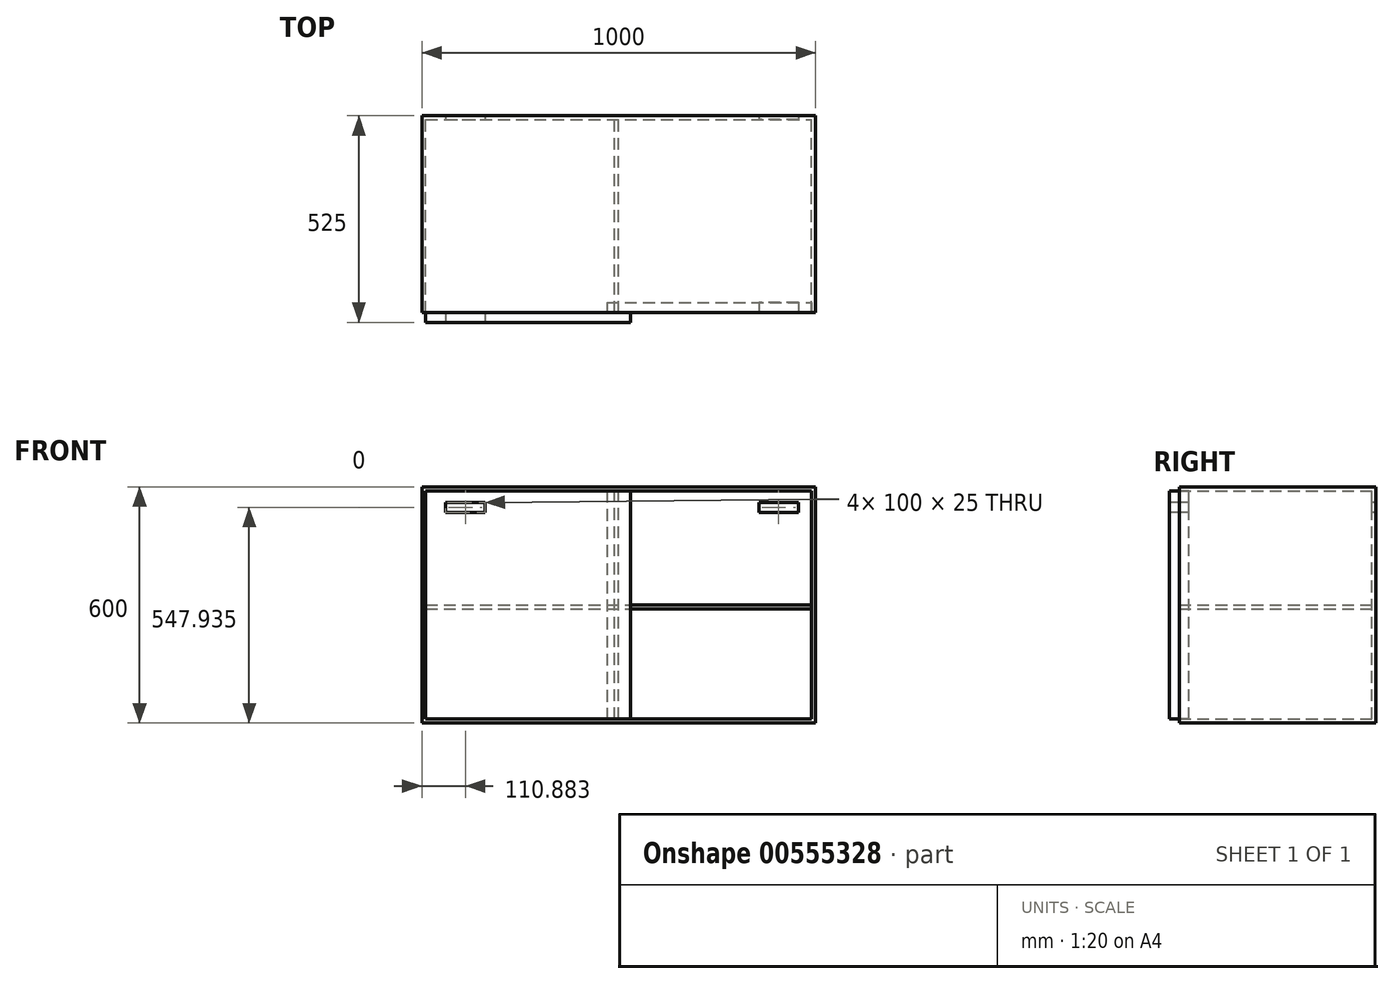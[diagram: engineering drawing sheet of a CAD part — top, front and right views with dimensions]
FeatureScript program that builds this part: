
annotation { "Feature Type Name" : "Feature", "Feature Type Description" : "" }
export const myFeature = defineFeature(function(context is Context, id is Id, definition is map)
    precondition{}
    {
        {
            var Q0;
            Q0=qCreatedBy(makeId("Front.planeOp"),FACE);
            var sketch = newSketch(context, id + "F0", { "sketchPlane" : qUnion([Q0])});
            skLineSegment(sketch, "E0.bottom", {"start": v(0, 0) * mm, "end": v(1000, 0) * mm});
            skLineSegment(sketch, "E0.top", {"start": v(0, 600) * mm, "end": v(1000, 600) * mm});
            skLineSegment(sketch, "E0.left", {"start": v(0, 0) * mm, "end": v(0, 600) * mm});
            skLineSegment(sketch, "E0.right", {"start": v(1000, 0) * mm, "end": v(1000, 600) * mm});
            skSolve(sketch);
        }
        {
            var Q0;
            Q0 = qSketchRegion(id + "F0", true);
            extrude(context, id + "F1", {"entities" : qUnion([Q0]), "depth" : 500 * mm, "offsetDistance" : 25 * mm});
        }
        {
            var Q0;
            Q0=makeQuery(id+"F1.opExtrude","CAP_FACE",FACE,{"disambiguationData":[OSD([sQuery(id+"F0.wireOp",EDGE,"E0.bottom"),sQuery(id+"F0.wireOp",EDGE,"E0.top"),sQuery(id+"F0.wireOp",EDGE,"E0.left"),sQuery(id+"F0.wireOp",EDGE,"E0.right")])],"isStart":false});
            shell(context, id + "F2", {"entities" : qUnion([Q0]), "thickness" : 10 * mm});
        }
        {
            var Q0;
            Q0=makeQuery(id+"F1.opExtrude","CAP_FACE",FACE,{"disambiguationData":[OSD([sQuery(id+"F0.wireOp",EDGE,"E0.bottom"),sQuery(id+"F0.wireOp",EDGE,"E0.top"),sQuery(id+"F0.wireOp",EDGE,"E0.left"),sQuery(id+"F0.wireOp",EDGE,"E0.right")])],"isStart":false});
            var sketch = newSketch(context, id + "F3", { "sketchPlane" : qUnion([Q0])});
            skLineSegment(sketch, "E1.bottom", {"start": v(10, 590) * mm, "end": v(530, 590) * mm});
            skLineSegment(sketch, "E1.top", {"start": v(10, 10) * mm, "end": v(530, 10) * mm});
            skLineSegment(sketch, "E1.left", {"start": v(10, 590) * mm, "end": v(10, 10) * mm});
            skLineSegment(sketch, "E1.right", {"start": v(530, 590) * mm, "end": v(530, 10) * mm});
            skLineSegment(sketch, "E2.bottom", {"start": v(990, 590) * mm, "end": v(470, 590) * mm});
            skLineSegment(sketch, "E2.top", {"start": v(990, 10) * mm, "end": v(470, 10) * mm});
            skLineSegment(sketch, "E2.left", {"start": v(990, 590) * mm, "end": v(990, 10) * mm});
            skLineSegment(sketch, "E2.right", {"start": v(470, 590) * mm, "end": v(470, 10) * mm});
            skSolve(sketch);
        }
        {
            var Q0;
            Q0=makeQuery(id+"F3.imprint","IMPRINT",FACE,{"disambiguationData":[TD([[makeQuery(id+"F3.imprint","IMPRINT",EDGE,{"derivedFrom":sQuery(id+"F3.wireOp",EDGE,"E1.bottom")}),-1.0]])]});
            var Q1;
            {var subQ0=sQuery(id+"F3.wireOp",EDGE,"E1.right");Q1=makeQuery(id+"F3.imprint","IMPRINT",FACE,{"disambiguationData":[TD([[makeQuery(id+"F3.imprint","IMPRINT",EDGE,{"derivedFrom":subQ0}),-1.0]])]});}
            extrude(context, id + "F4", {"entities" : qUnion([Q0, Q1]), "depth" : 25 * mm, "offsetDistance" : 25 * mm});
        }
        {
            var Q0;
            {var subQ0=sQuery(id+"F3.wireOp",EDGE,"E1.right");Q0=makeQuery(id+"F3.imprint","IMPRINT",FACE,{"disambiguationData":[TD([[makeQuery(id+"F3.imprint","IMPRINT",EDGE,{"derivedFrom":subQ0}),1.0]])]});}
            var Q1;
            {var subQ0=sQuery(id+"F3.wireOp",EDGE,"E1.right");Q1=makeQuery(id+"F3.imprint","IMPRINT",FACE,{"disambiguationData":[TD([[makeQuery(id+"F3.imprint","IMPRINT",EDGE,{"derivedFrom":subQ0}),-1.0]])]});}
            extrude(context, id + "F5", {"entities" : qUnion([Q0, Q1]), "oppositeDirection" : true, "depth" : 25 * mm, "offsetDistance" : 25 * mm});
        }
        {
            var Q0;
            Q0=makeQuery(id+"F4.opExtrude","CAP_FACE",FACE,{"disambiguationData":[OSD([sQuery(id+"F3.wireOp",EDGE,"E1.bottom"),sQuery(id+"F3.wireOp",EDGE,"E1.top"),sQuery(id+"F3.wireOp",EDGE,"E1.left"),sQuery(id+"F3.wireOp",EDGE,"E1.right"),sQuery(id+"F3.wireOp",EDGE,"E2.bottom"),sQuery(id+"F3.wireOp",EDGE,"E2.top")])],"isStart":false});
            var sketch = newSketch(context, id + "F6", { "sketchPlane" : qUnion([Q0])});
            skLineSegment(sketch, "E3.bottom", {"start": v(60.88, 560.44) * mm, "end": v(160.88, 560.44) * mm});
            skLineSegment(sketch, "E3.top", {"start": v(60.88, 535.44) * mm, "end": v(160.88, 535.44) * mm});
            skLineSegment(sketch, "E3.left", {"start": v(60.88, 560.44) * mm, "end": v(60.88, 535.44) * mm});
            skLineSegment(sketch, "E3.right", {"start": v(160.88, 560.44) * mm, "end": v(160.88, 535.44) * mm});
            skLineSegment(sketch, "E4.bottom", {"start": v(956.4, 535.44) * mm, "end": v(856.4, 535.44) * mm});
            skLineSegment(sketch, "E4.top", {"start": v(956.4, 560.44) * mm, "end": v(856.4, 560.44) * mm});
            skLineSegment(sketch, "E4.left", {"start": v(956.4, 535.44) * mm, "end": v(956.4, 560.44) * mm});
            skLineSegment(sketch, "E4.right", {"start": v(856.4, 535.44) * mm, "end": v(856.4, 560.44) * mm});
            skSolve(sketch);
        }
        {
            var Q0;
            Q0=makeQuery(id+"F6.imprint","IMPRINT",FACE,{"disambiguationData":[TD([[makeQuery(id+"F6.imprint","IMPRINT",EDGE,{"derivedFrom":sQuery(id+"F6.wireOp",EDGE,"E3.bottom")}),-1.0]])]});
            var Q1;
            Q1=makeQuery(id+"F6.imprint","IMPRINT",FACE,{"disambiguationData":[TD([[makeQuery(id+"F6.imprint","IMPRINT",EDGE,{"derivedFrom":sQuery(id+"F6.wireOp",EDGE,"E4.bottom")}),-1.0]])]});
            extrude(context, id + "F7", {"entities" : qUnion([Q0, Q1]), "operationType" : NewBodyOperationType.REMOVE, "endBound" : BoundingType.THROUGH_ALL, "oppositeDirection" : true, "depth" : 25 * mm, "offsetDistance" : 25 * mm, "hasSecondDirection" : true, "secondDirectionBound" : SecondDirectionBoundingType.THROUGH_ALL, "secondDirectionOppositeDirection" : false, "secondDirectionDepth" : 25 * mm});
        }
        {
            var Q0;
            Q0=makeQuery(id+"F2.opShell","OFFSET_FACE",FACE,{"disambiguationData":[OSD([sQuery(id+"F0.wireOp",EDGE,"E0.bottom"),sQuery(id+"F0.wireOp",EDGE,"E0.top"),sQuery(id+"F0.wireOp",EDGE,"E0.left"),sQuery(id+"F0.wireOp",EDGE,"E0.right")])]});
            var sketch = newSketch(context, id + "F8", { "sketchPlane" : qUnion([Q0])});
            skLineSegment(sketch, "E5.bottom", {"start": v(10, 300) * mm, "end": v(990, 300) * mm});
            skLineSegment(sketch, "E5.top", {"start": v(10, 290) * mm, "end": v(990, 290) * mm});
            skLineSegment(sketch, "E5.left", {"start": v(10, 300) * mm, "end": v(10, 290) * mm});
            skLineSegment(sketch, "E5.right", {"start": v(990, 300) * mm, "end": v(990, 290) * mm});
            skSolve(sketch);
        }
        {
            var Q0;
            Q0 = qSketchRegion(id + "F8", true);
            var Q1;
            Q1=makeQuery(id+"F1.opExtrude","CAP_FACE",FACE,{"disambiguationData":[OSD([sQuery(id+"F0.wireOp",EDGE,"E0.bottom"),sQuery(id+"F0.wireOp",EDGE,"E0.top"),sQuery(id+"F0.wireOp",EDGE,"E0.left"),sQuery(id+"F0.wireOp",EDGE,"E0.right")])],"isStart":false});
            extrude(context, id + "F9", {"entities" : qUnion([Q0]), "endBound" : BoundingType.UP_TO_SURFACE, "depth" : 25 * mm, "endBoundEntityFace" : qUnion([Q1]), "offsetDistance" : 25 * mm});
        }
        {
            var Q0;
            Q0=makeQuery(id+"F2.opShell","OFFSET_FACE",FACE,{"disambiguationData":[OSD([sQuery(id+"F0.wireOp",EDGE,"E0.bottom"),sQuery(id+"F0.wireOp",EDGE,"E0.top"),sQuery(id+"F0.wireOp",EDGE,"E0.left"),sQuery(id+"F0.wireOp",EDGE,"E0.right")])]});
            var sketch = newSketch(context, id + "F10", { "sketchPlane" : qUnion([Q0])});
            skLineSegment(sketch, "E6.bottom", {"start": v(500, 10) * mm, "end": v(490, 10) * mm});
            skLineSegment(sketch, "E6.top", {"start": v(500, 590) * mm, "end": v(490, 590) * mm});
            skLineSegment(sketch, "E6.left", {"start": v(500, 10) * mm, "end": v(500, 590) * mm});
            skLineSegment(sketch, "E6.right", {"start": v(490, 10) * mm, "end": v(490, 590) * mm});
            skSolve(sketch);
        }
        {
            var Q0;
            Q0=makeQuery(id+"F10.imprint","IMPRINT",FACE,{"disambiguationData":[TD([[makeQuery(id+"F10.imprint","IMPRINT",EDGE,{"derivedFrom":sQuery(id+"F10.wireOp",EDGE,"E6.bottom")}),1.0]])]});
            var Q1;
            Q1=makeQuery(id+"F1.opExtrude","CAP_FACE",FACE,{"disambiguationData":[OSD([sQuery(id+"F0.wireOp",EDGE,"E0.bottom"),sQuery(id+"F0.wireOp",EDGE,"E0.top"),sQuery(id+"F0.wireOp",EDGE,"E0.left"),sQuery(id+"F0.wireOp",EDGE,"E0.right")])],"isStart":false});
            extrude(context, id + "F11", {"entities" : qUnion([Q0]), "endBound" : BoundingType.UP_TO_SURFACE, "depth" : 25 * mm, "endBoundEntityFace" : qUnion([Q1]), "offsetDistance" : 25 * mm});
        }
    });
